# Revit family: Door-Hardware_Accessories_Hager_Power-Supply-Cabinet
name_source: partatom
category: Specialty Equipment
units: mm (PartAtom-declared; Revit-internal decimal feet)

## family parameters
Always vertical = No
Classification Number = 23.30.40.00
Cut with Voids When Loaded = No
Enable Cutting in Views = No
Maintain Annotation Orientation = No
Part Type = Normal
Room Calculation Point = No
Round Connector Dimension = Use Diameter
Shared = Yes
Work Plane-Based = Yes

## types (6) — shared parameters
Assembly Code = C1020410
Capacity = as Specified
Default Elevation = 0' - 0"
Keynote = 087100
Manufacturer = Hager Companies
Manufacturer Fax = 800-782-0149
Manufacturer Website = http://www.hagerco.com
Operating Temperature Range = Interior - Exterior
Product Data = http://www.arcat.com
Revision = R1_2015-10
Sales Information = http://www.hagerco.com
Specification = http://www.arcat.com
Standards Conformance = California Compliant Manual Release with Proper Options
URL = http://www.hagerco.com
zero-valued in all types: Expected Lifespan (Years), Maintenance Schedule (Months), Warranty Duration (Years)

## per-type parameters (varying)
| type | Description | Model |
| 2A Modular Access | Hager Power Supply Cabinet - 2909 as Specified | 2909 |
| 1A Modular Access | Hager Power Supply Cabinet - 2908 as Specified | 2908 |
| Fail Safe and Fail Secure Power with Fire Alarm Input | Hager Power Supply Cabinet - 2904 as Specified | 2904 |
| Fail Safe and Fail Secure Power | Hager Power Supply Cabinet - 2903 as Specified | 2903 |
| Simultaneous ELR Operation Day Night | Hager Power Supply Cabinet - 2902 as Specified | 2902 |
| Independent or Simultaneous ELR Operation | Hager Power Supply Cabinet - 2901 as Specified | 2901 |

## geometry (parser evidence)
native form markers: Blend x6, Sweep x2
no freeform markers — native parametric forms only
